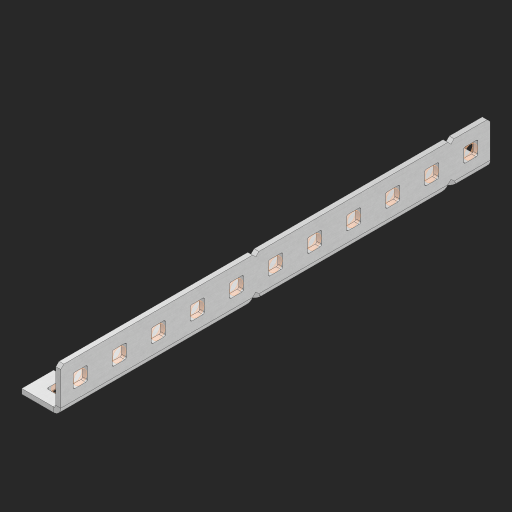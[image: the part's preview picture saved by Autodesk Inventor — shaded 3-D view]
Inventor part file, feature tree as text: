
AUTODESK INVENTOR PART (.ipt)
format: ipt  version: 2023 (Build 270158000, 158)  size: 747,008 bytes
history: native  units: in
note: dims shown in document units (in); Inventor stores cm internally (conversion verified against a paired STEP export)
features: other x181, extrude x31, sheet_metal_op x11, sketch x10, pattern_linear x2, mirror x1, chamfer x1
ambient origin geometry x8: Origin, YZ Plane, XZ Plane, XY Plane, X Axis, Y Axis, Z Axis, Center Point
bodies: Solid1 (feature_tree), Body (feature_tree)
feature tree (237):
  other  "Alu Half C 1x2x1x11"
  other  "Table"
  other  "Alu C 1x2x1x35"
  other  "Alu C 1x2x1x34"
  other  "Alu C 1x2x1x33"
  other  "Alu C 1x2x1x32"
  other  "Alu C 1x2x1x31"
  other  "Alu C 1x2x1x30"
  other  "Alu C 1x2x1x29"
  other  "Alu C 1x2x1x28"
  other  "Alu C 1x2x1x27"
  other  "Alu C 1x2x1x26"
  other  "Alu C 1x2x1x25"
  other  "Alu C 1x2x1x24"
  other  "Alu C 1x2x1x23"
  other  "Alu C 1x2x1x22"
  other  "Alu C 1x2x1x21"
  other  "Alu C 1x2x1x20"
  other  "Alu C 1x2x1x19"
  other  "Alu C 1x2x1x18"
  other  "Alu C 1x2x1x17"
  other  "Alu C 1x2x1x16"
  other  "Alu C 1x2x1x15"
  other  "Alu C 1x2x1x14"
  other  "Alu C 1x2x1x13"
  other  "Alu C 1x2x1x12"
  other  "Alu C 1x2x1x11"
  other  "Alu C 1x2x1x10"
  other  "Alu C 1x2x1x9"
  other  "Alu C 1x2x1x8"
  other  "Alu C 1x2x1x7"
  other  "Alu C 1x2x1x6"
  other  "Alu C 1x2x1x5"
  other  "Alu C 1x2x1x4"
  other  "Alu C 1x2x1x3"
  other  "Alu C 1x2x1x2"
  other  "Alu C 1x2x1x1"
  other  "Steel C 1x2x1x35"
  other  "Steel C 1x2x1x34"
  other  "Steel C 1x2x1x33"
  other  "Steel C 1x2x1x32"
  other  "Steel C 1x2x1x31"
  other  "Steel C 1x2x1x30"
  other  "Steel C 1x2x1x29"
  other  "Steel C 1x2x1x28"
  other  "Steel C 1x2x1x27"
  other  "Steel C 1x2x1x26"
  other  "Steel C 1x2x1x25"
  other  "Steel C 1x2x1x24"
  other  "Steel C 1x2x1x23"
  other  "Steel C 1x2x1x22"
  other  "Steel C 1x2x1x21"
  other  "Steel C 1x2x1x20"
  other  "Steel C 1x2x1x19"
  other  "Steel C 1x2x1x18"
  other  "Steel C 1x2x1x17"
  other  "Steel C 1x2x1x16"
  other  "Steel C 1x2x1x15"
  other  "Steel C 1x2x1x14"
  other  "Steel C 1x2x1x13"
  other  "Steel C 1x2x1x12"
  other  "Steel C 1x2x1x11"
  other  "Steel C 1x2x1x10"
  other  "Steel C 1x2x1x9"
  other  "Steel C 1x2x1x8"
  other  "Steel C 1x2x1x7"
  other  "Steel C 1x2x1x6"
  other  "Steel C 1x2x1x5"
  other  "Steel C 1x2x1x4"
  other  "Steel C 1x2x1x3"
  other  "Steel C 1x2x1x2"
  other  "Steel C 1x2x1x1"
  other  "Alu Half C 1x2x1x35"
  other  "Alu Half C 1x2x1x34"
  other  "Alu Half C 1x2x1x33"
  other  "Alu Half C 1x2x1x32"
  other  "Alu Half C 1x2x1x31"
  other  "Alu Half C 1x2x1x30"
  other  "Alu Half C 1x2x1x29"
  other  "Alu Half C 1x2x1x28"
  other  "Alu Half C 1x2x1x27"
  other  "Alu Half C 1x2x1x26"
  other  "Alu Half C 1x2x1x25"
  other  "Alu Half C 1x2x1x24"
  other  "Alu Half C 1x2x1x23"
  other  "Alu Half C 1x2x1x22"
  other  "Alu Half C 1x2x1x21"
  other  "Alu Half C 1x2x1x20"
  other  "Alu Half C 1x2x1x19"
  other  "Alu Half C 1x2x1x18"
  other  "Alu Half C 1x2x1x17"
  other  "Alu Half C 1x2x1x16"
  other  "Alu Half C 1x2x1x15"
  other  "Alu Half C 1x2x1x14"
  other  "Alu Half C 1x2x1x13"
  other  "Alu Half C 1x2x1x12"
  other  "Alu Half C 1x2x1x10"
  other  "Alu Half C 1x2x1x9"
  other  "Alu Half C 1x2x1x8"
  other  "Alu Half C 1x2x1x7"
  other  "Alu Half C 1x2x1x6"
  other  "Alu Half C 1x2x1x5"
  other  "Alu Half C 1x2x1x4"
  other  "Alu Half C 1x2x1x3"
  other  "Alu Half C 1x2x1x2"
  other  "Alu Half C 1x2x1x1"
  other  "Steel Half C 1x2x1x35"
  other  "Steel Half C 1x2x1x34"
  other  "Steel Half C 1x2x1x33"
  other  "Steel Half C 1x2x1x32"
  other  "Steel Half C 1x2x1x31"
  other  "Steel Half C 1x2x1x30"
  other  "Steel Half C 1x2x1x29"
  other  "Steel Half C 1x2x1x28"
  other  "Steel Half C 1x2x1x27"
  other  "Steel Half C 1x2x1x26"
  other  "Steel Half C 1x2x1x25"
  other  "Steel Half C 1x2x1x24"
  other  "Steel Half C 1x2x1x23"
  other  "Steel Half C 1x2x1x22"
  other  "Steel Half C 1x2x1x21"
  other  "Steel Half C 1x2x1x20"
  other  "Steel Half C 1x2x1x19"
  other  "Steel Half C 1x2x1x18"
  other  "Steel Half C 1x2x1x17"
  other  "Steel Half C 1x2x1x16"
  other  "Steel Half C 1x2x1x15"
  other  "Steel Half C 1x2x1x14"
  other  "Steel Half C 1x2x1x13"
  other  "Steel Half C 1x2x1x12"
  other  "Steel Half C 1x2x1x11"
  other  "Steel Half C 1x2x1x10"
  other  "Steel Half C 1x2x1x9"
  other  "Steel Half C 1x2x1x8"
  other  "Steel Half C 1x2x1x7"
  other  "Steel Half C 1x2x1x6"
  other  "Steel Half C 1x2x1x5"
  other  "Steel Half C 1x2x1x4"
  other  "Steel Half C 1x2x1x3"
  other  "Steel Half C 1x2x1x2"
  other  "Steel Half C 1x2x1x1"
  sheet_metal_op  "Flanges"
  other  "Flange Pattern Plane"
  other  "Flange Pattern Sketch"
  sheet_metal_op  "Flange Pattern"
  sheet_metal_op  "Body Pattern"
  pattern_linear  "Center Pattern"  Spacing1=0.0625in  [1 undecoded]
  other  "Arc Length"
  mirror  "Notch Mirror"
  pattern_linear  "Notch Pattern"  Spacing1=0.182in  [1 undecoded]
  chamfer  "End Chamfer"
  extrude  "Half Cut"  Depth=0.02in
  sketch  "Sketch1"  dims[d0=1.0in]
  other  "Plate1"
  sketch  "Sketch2"  dims[d1=5.5in]
  other  "Plate2"
  sheet_metal_op  "Bend1"
  sheet_metal_op  "Corner1"
  sketch  "Sketch3"  dims[d2=0.0625in]
  sketch  "Sketch7"  dims[d3=0.0625in]
  other  "Srf1"
  other  "Srf2"
  sketch  "Sketch8"  dims[d4=0.0312in]
  sketch  "Sketch9"  dims[d5=0.125in]
  other  "Srf91"
  sheet_metal_op  "Body Pattern Sketch"
  other  "Srf92"
  sketch  "Sketch13"  dims[d6=0.0625in]
  sketch  "Sketch14"  dims[d7=0.5in d8=90.0deg d9=0.0312in]
  sketch  "Sketch15"  dims[d10=0.25in]
  sketch  "Sketch16"  dims[d11=0.0625in d12=0.0625in d16=0.182in d17=0.02in d18=0.0625in d19=0.0in d20=0.25in d21=0.25in d38=4.3307in d40=0.5in d41=0.3937in d43=1.0in d46=0.172in d47=1.0in d48=0.0in d49=0.182in d50=0.02in d51=0.25in d52=0.25in d53=0.0625in d54=0.0in d55=0.172in d56=1.0in d57=0.0in d58=0.25in d60=4.3307in d62=0.5in d63=0.3937in d65=0.5in d85=0.1473in d86=0.1782in d88=0.04in d89=0.0625in d90=0.0in d91=0.04in d92=0.0491in d95=2.5in d96=0.04in d97=0.25in d98=45.0deg d99=0.25in d100=0.5in d101=0.0in d102=2.497in d106=0.182in d107=0.02in d108=0.5in d109=0.5in d110=0.0625in d111=0.0in d112=0.172in d113=0.5in d114=0.0in d117=0.5in d118=0.5in d119=0.5in]
  other  "Srf786"
  other  "Srf823"
  other  "Srf824"
  other  "Srf825"
  other  "Srf826"
  other  "Srf827"
  other  "Srf828"
  other  "Srf829"
  other  "Srf856"
  other  "Srf857"
  other  "Srf858"
  other  "Srf859"
  other  "Srf860"
  other  "Srf861"
  other  "Srf862"
  other  "Srf889"
  other  "Srf890"
  other  "Srf891"
  other  "Srf892"
  other  "Srf893"
  other  "Srf894"
  other  "Srf895"
  other  "Srf896"
  other  "Srf922"
  other  "Srf923"
  other  "Srf959"
  other  "Srf960"
  other  "Srf996"
  other  "Srf997"
  sheet_metal_op  "Flange Stamp"
  sheet_metal_op  "Flange Circle"
  sheet_metal_op  "Body Stamp"
  sheet_metal_op  "Body Circle"
  other  "Center Stamp"
  other  "Center Circle"
  sheet_metal_op  "Notch"
  extrude  "ExtrusionSrf2"  Depth=0.0625in
  extrude  "ExtrusionSrf92"  TaperAngle=0.0deg  [1 undecoded]
  extrude  "ExtrusionSrf823"  Depth=0.5in
  extrude  "ExtrusionSrf824"  Depth=0.5in
  extrude  "ExtrusionSrf825"  Depth=0.5in
  extrude  "ExtrusionSrf826"  Depth=0.5in
  extrude  "ExtrusionSrf827"  Depth=1.0in TaperAngle=0.0deg
  extrude  "ExtrusionSrf828"  Depth=0.182in
  extrude  "ExtrusionSrf829"  Depth=0.02in
  extrude  "ExtrusionSrf856"  Depth=0.5in
  extrude  "ExtrusionSrf857"  Depth=0.5in
  extrude  "ExtrusionSrf858"  Depth=0.0625in
  extrude  "ExtrusionSrf859"  TaperAngle=0.0deg  [1 undecoded]
  extrude  "ExtrusionSrf860"  Depth=0.5in
  extrude  "ExtrusionSrf861"  Depth=1.0in TaperAngle=0.0deg
  extrude  "ExtrusionSrf862"  Depth=0.5in
  extrude  "ExtrusionSrf889"  Depth=0.5in
  extrude  "ExtrusionSrf890"  Depth=0.5in
  extrude  "ExtrusionSrf891"  Depth=0.5in
  extrude  "ExtrusionSrf892"  Depth=0.5in
  extrude  "ExtrusionSrf893"  Depth=0.5in
  extrude  "ExtrusionSrf894"  Depth=0.0625in
  extrude  "ExtrusionSrf895"  TaperAngle=0.0deg  [1 undecoded]
  extrude  "ExtrusionSrf896"  Depth=0.5in
  extrude  "ExtrusionSrf922"  Depth=0.5in
  extrude  "ExtrusionSrf923"  Depth=2.5in
  extrude  "ExtrusionSrf959"  Depth=0.5in TaperAngle=45.0deg
  extrude  "ExtrusionSrf960"  Depth=0.5in
  extrude  "ExtrusionSrf996"  Depth=0.5in TaperAngle=0.0deg
  extrude  "ExtrusionSrf997"  Depth=0.5in
note: 5 required parameter values undecoded (feature->parameter linkage not recoverable at this tier; creation-order binding heuristic only, values carry confidence <= 0.55)
